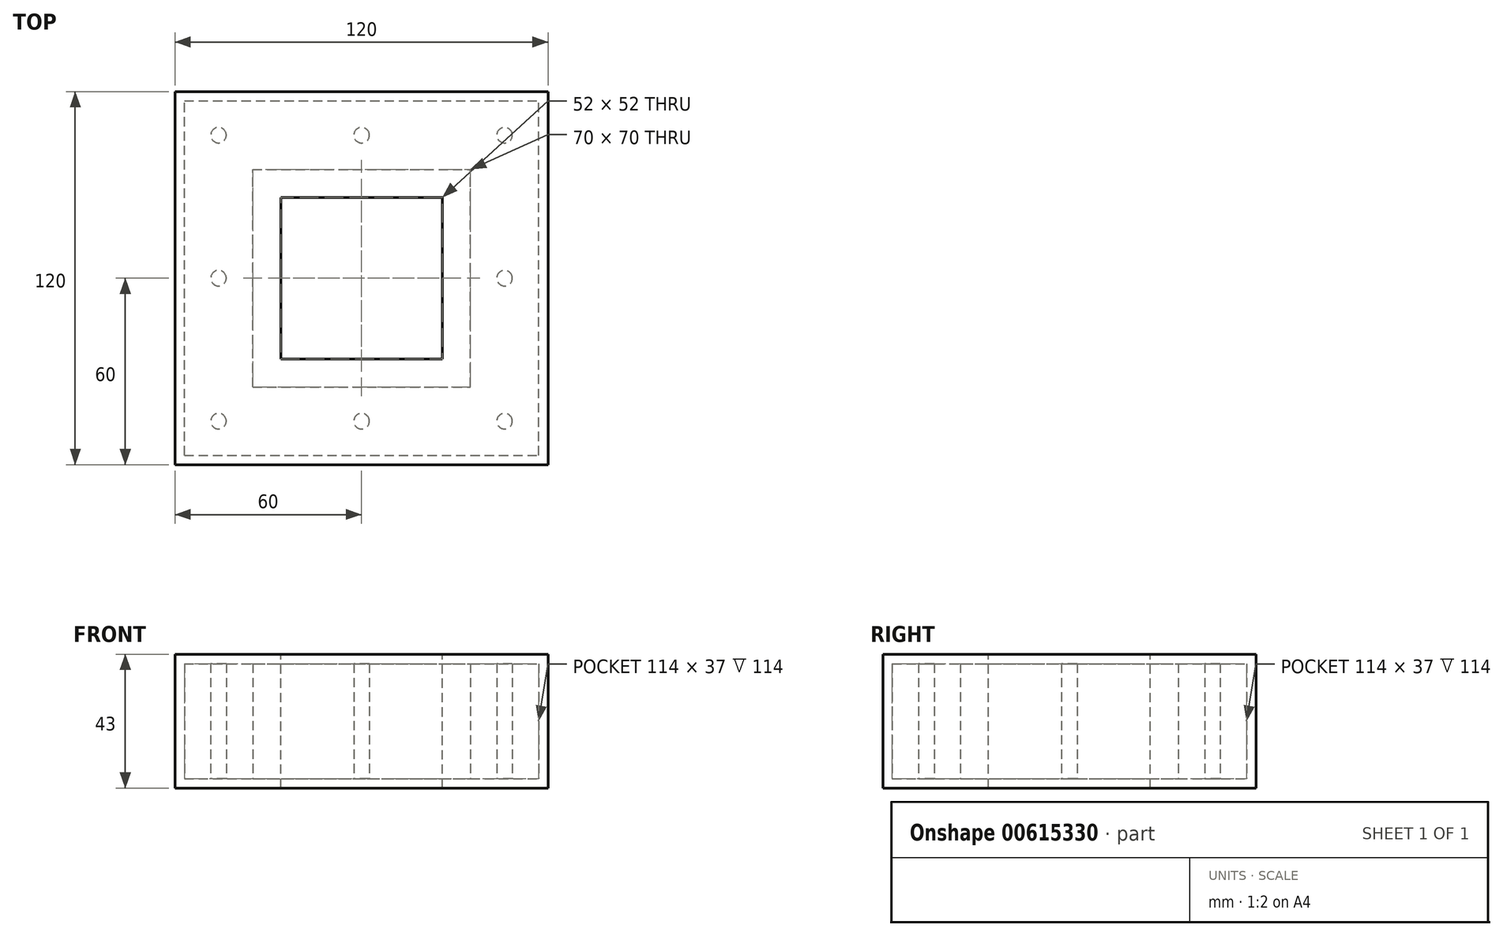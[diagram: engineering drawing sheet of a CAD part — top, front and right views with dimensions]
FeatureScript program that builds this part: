
annotation { "Feature Type Name" : "Feature", "Feature Type Description" : "" }
export const myFeature = defineFeature(function(context is Context, id is Id, definition is map)
    precondition{}
    {
        {
            var Q0;
            Q0=qCreatedBy(makeId("Top.planeOp"),FACE);
            var sketch = newSketch(context, id + "F0", { "sketchPlane" : qUnion([Q0])});
            skLineSegment(sketch, "E0.bottom", {"start": v(-60, -60) * mm, "end": v(60, -60) * mm});
            skLineSegment(sketch, "E0.top", {"start": v(-60, 60) * mm, "end": v(60, 60) * mm});
            skLineSegment(sketch, "E0.left", {"start": v(-60, -60) * mm, "end": v(-60, 60) * mm});
            skLineSegment(sketch, "E0.right", {"start": v(60, -60) * mm, "end": v(60, 60) * mm});
            skPoint(sketch, "E0.middle", {"position": v(0, 0) * mm});
            skSolve(sketch);
        }
        {
            var Q0;
            Q0 = qSketchRegion(id + "F0", true);
            extrude(context, id + "F1", {"entities" : qUnion([Q0]), "depth" : 3 * mm, "offsetDistance" : 25 * mm});
        }
        {
            var Q0;
            Q0=makeQuery(id+"F1.opExtrude","CAP_FACE",FACE,{"disambiguationData":[OSD([sQuery(id+"F0.wireOp",EDGE,"E0.bottom"),sQuery(id+"F0.wireOp",EDGE,"E0.top"),sQuery(id+"F0.wireOp",EDGE,"E0.left"),sQuery(id+"F0.wireOp",EDGE,"E0.right")])],"isStart":false});
            var sketch = newSketch(context, id + "F2", { "sketchPlane" : qUnion([Q0])});
            skLineSegment(sketch, "E1.bottom", {"start": v(-26, -26) * mm, "end": v(26, -26) * mm});
            skLineSegment(sketch, "E1.top", {"start": v(-26, 26) * mm, "end": v(26, 26) * mm});
            skLineSegment(sketch, "E1.left", {"start": v(-26, -26) * mm, "end": v(-26, 26) * mm});
            skLineSegment(sketch, "E1.right", {"start": v(26, -26) * mm, "end": v(26, 26) * mm});
            skPoint(sketch, "E1.middle", {"position": v(0, 0) * mm});
            skLineSegment(sketch, "E2.bottom", {"start": v(-35, -35) * mm, "end": v(35, -35) * mm});
            skLineSegment(sketch, "E2.top", {"start": v(-35, 35) * mm, "end": v(35, 35) * mm});
            skLineSegment(sketch, "E2.left", {"start": v(-35, -35) * mm, "end": v(-35, 35) * mm});
            skLineSegment(sketch, "E2.right", {"start": v(35, -35) * mm, "end": v(35, 35) * mm});
            skLineSegment(sketch, "E3.bottom", {"start": v(-57, -57) * mm, "end": v(57, -57) * mm});
            skLineSegment(sketch, "E3.top", {"start": v(-57, 57) * mm, "end": v(57, 57) * mm});
            skLineSegment(sketch, "E3.left", {"start": v(-57, -57) * mm, "end": v(-57, 57) * mm});
            skLineSegment(sketch, "E3.right", {"start": v(57, -57) * mm, "end": v(57, 57) * mm});
            skLineSegment(sketch, "E4", {"start": v(-57, 35) * mm, "end": v(-57, 57) * mm});
            skLineSegment(sketch, "E5", {"start": v(-35, 57) * mm, "end": v(-57, 57) * mm});
            skLineSegment(sketch, "E6", {"start": v(35, 35) * mm, "end": v(57, 35) * mm});
            skLineSegment(sketch, "E7", {"start": v(57, 35) * mm, "end": v(57, 57) * mm});
            skLineSegment(sketch, "E8", {"start": v(35, 57) * mm, "end": v(57, 57) * mm});
            skLineSegment(sketch, "E9", {"start": v(35, -35) * mm, "end": v(57, -35) * mm});
            skLineSegment(sketch, "E10", {"start": v(57, -35) * mm, "end": v(57, -57) * mm});
            skLineSegment(sketch, "E11", {"start": v(57, -57) * mm, "end": v(35, -57) * mm});
            skLineSegment(sketch, "E12", {"start": v(-35, -35) * mm, "end": v(-57, -35) * mm});
            skLineSegment(sketch, "E13", {"start": v(-57, -35) * mm, "end": v(-57, -57) * mm});
            skLineSegment(sketch, "E14", {"start": v(-57, -57) * mm, "end": v(-35, -57) * mm});
            skPoint(sketch, "E15", {"position": v(-46, 46) * mm});
            skPoint(sketch, "E15.positionSnap0", {"position": v(-57, 46) * mm});
            skPoint(sketch, "E15.positionSnap1", {"position": v(-46, 57) * mm});
            skPoint(sketch, "E16", {"position": v(46, 46) * mm});
            skPoint(sketch, "E16.positionSnap0", {"position": v(57, 46) * mm});
            skPoint(sketch, "E16.positionSnap1", {"position": v(46, 57) * mm});
            skPoint(sketch, "E17", {"position": v(46, -46) * mm});
            skPoint(sketch, "E17.positionSnap0", {"position": v(57, -46) * mm});
            skPoint(sketch, "E17.positionSnap1", {"position": v(46, 35) * mm});
            skPoint(sketch, "E18", {"position": v(-46, -46) * mm});
            skPoint(sketch, "E18.positionSnap0", {"position": v(-46, -57) * mm});
            skPoint(sketch, "E18.positionSnap1", {"position": v(-57, -46) * mm});
            skPoint(sketch, "E19", {"position": v(0, -46) * mm});
            skPoint(sketch, "E19.positionSnap0", {"position": v(0, -57) * mm});
            skPoint(sketch, "E20", {"position": v(0, 46) * mm});
            skPoint(sketch, "E20.positionSnap0", {"position": v(0, 57) * mm});
            skCircle(sketch, "E21", {"center": v(-46, 46) * mm, "radius": 2.5 * mm});
            skCircle(sketch, "E22", {"center": v(0, 46) * mm, "radius": 2.5 * mm});
            skCircle(sketch, "E23", {"center": v(46, 46) * mm, "radius": 2.5 * mm});
            skCircle(sketch, "E24", {"center": v(46, -46) * mm, "radius": 2.5 * mm});
            skCircle(sketch, "E25", {"center": v(0, -46) * mm, "radius": 2.5 * mm});
            skCircle(sketch, "E26", {"center": v(-46, -46) * mm, "radius": 2.5 * mm});
            skCircle(sketch, "E27", {"center": v(46, 0) * mm, "radius": 2.5 * mm});
            skCircle(sketch, "E28", {"center": v(-46, 0) * mm, "radius": 2.5 * mm});
            skSolve(sketch);
        }
        {
            var Q0;
            Q0=makeQuery(id+"F2.imprint","IMPRINT",FACE,{"disambiguationData":[TD([[makeQuery(id+"F2.imprint","IMPRINT",EDGE,{"derivedFrom":sQuery(id+"F2.wireOp",EDGE,"E1.bottom")}),1.0]])]});
            extrude(context, id + "F3", {"entities" : qUnion([Q0]), "operationType" : NewBodyOperationType.REMOVE, "oppositeDirection" : true, "depth" : 25 * mm, "offsetDistance" : 25 * mm});
        }
        {
            var Q0;
            Q0=makeQuery(id+"F2.imprint","IMPRINT",FACE,{"disambiguationData":[TD([[makeQuery(id+"F2.imprint","IMPRINT",EDGE,{"derivedFrom":sQuery(id+"F2.wireOp",EDGE,"E23")}),1.0]])]});
            var Q1;
            Q1=makeQuery(id+"F2.imprint","IMPRINT",FACE,{"disambiguationData":[TD([[makeQuery(id+"F2.imprint","IMPRINT",EDGE,{"derivedFrom":sQuery(id+"F2.wireOp",EDGE,"E22")}),1.0]])]});
            var Q2;
            Q2=makeQuery(id+"F2.imprint","IMPRINT",FACE,{"disambiguationData":[TD([[makeQuery(id+"F2.imprint","IMPRINT",EDGE,{"derivedFrom":sQuery(id+"F2.wireOp",EDGE,"E21")}),1.0]])]});
            var Q3;
            Q3=makeQuery(id+"F2.imprint","IMPRINT",FACE,{"disambiguationData":[TD([[makeQuery(id+"F2.imprint","IMPRINT",EDGE,{"derivedFrom":sQuery(id+"F2.wireOp",EDGE,"E28")}),1.0]])]});
            var Q4;
            Q4=makeQuery(id+"F2.imprint","IMPRINT",FACE,{"disambiguationData":[TD([[makeQuery(id+"F2.imprint","IMPRINT",EDGE,{"derivedFrom":sQuery(id+"F2.wireOp",EDGE,"E26")}),1.0]])]});
            var Q5;
            Q5=makeQuery(id+"F2.imprint","IMPRINT",FACE,{"disambiguationData":[TD([[makeQuery(id+"F2.imprint","IMPRINT",EDGE,{"derivedFrom":sQuery(id+"F2.wireOp",EDGE,"E25")}),1.0]])]});
            var Q6;
            Q6=makeQuery(id+"F2.imprint","IMPRINT",FACE,{"disambiguationData":[TD([[makeQuery(id+"F2.imprint","IMPRINT",EDGE,{"derivedFrom":sQuery(id+"F2.wireOp",EDGE,"E24")}),1.0]])]});
            var Q7;
            Q7=makeQuery(id+"F2.imprint","IMPRINT",FACE,{"disambiguationData":[TD([[makeQuery(id+"F2.imprint","IMPRINT",EDGE,{"derivedFrom":sQuery(id+"F2.wireOp",EDGE,"E27")}),1.0]])]});
            var Q8;
            Q8=makeQuery(id+"F2.imprint","IMPRINT",FACE,{"disambiguationData":[TD([[makeQuery(id+"F2.imprint","IMPRINT",EDGE,{"derivedFrom":sQuery(id+"F2.wireOp",EDGE,"E3.bottom")}),-1.0]])]});
            var Q9;
            Q9=makeQuery(id+"F2.imprint","IMPRINT",FACE,{"disambiguationData":[TD([[makeQuery(id+"F2.imprint","IMPRINT",EDGE,{"derivedFrom":sQuery(id+"F2.wireOp",EDGE,"E1.bottom")}),-1.0]])]});
            extrude(context, id + "F4", {"entities" : qUnion([Q0, Q1, Q2, Q3, Q4, Q5, Q6, Q7, Q8, Q9]), "operationType" : NewBodyOperationType.ADD, "depth" : 37 * mm, "offsetDistance" : 25 * mm});
        }
        {
            var Q0;
            Q0=makeQuery(id+"F4.opExtrude","CAP_FACE",FACE,{"disambiguationData":[OSD([sQuery(id+"F0.wireOp",EDGE,"E0.bottom"),sQuery(id+"F0.wireOp",EDGE,"E0.top"),sQuery(id+"F0.wireOp",EDGE,"E0.left"),sQuery(id+"F0.wireOp",EDGE,"E0.right"),sQuery(id+"F2.wireOp",EDGE,"E3.bottom"),sQuery(id+"F2.wireOp",EDGE,"E3.top"),sQuery(id+"F2.wireOp",EDGE,"E3.left"),sQuery(id+"F2.wireOp",EDGE,"E3.right"),sQuery(id+"F2.wireOp",EDGE,"E4"),sQuery(id+"F2.wireOp",EDGE,"E7"),sQuery(id+"F2.wireOp",EDGE,"E8"),sQuery(id+"F2.wireOp",EDGE,"E5"),sQuery(id+"F2.wireOp",EDGE,"E10"),sQuery(id+"F2.wireOp",EDGE,"E11"),sQuery(id+"F2.wireOp",EDGE,"E13"),sQuery(id+"F2.wireOp",EDGE,"E14")])],"isStart":false});
            var sketch = newSketch(context, id + "F5", { "sketchPlane" : qUnion([Q0])});
            skPoint(sketch, "E29.middle", {"position": v(0, 0) * mm});
            skLineSegment(sketch, "E30", {"start": v(-60, 60) * mm, "end": v(-60, -60) * mm});
            skLineSegment(sketch, "E31", {"start": v(-60, -60) * mm, "end": v(60, -60) * mm});
            skLineSegment(sketch, "E32", {"start": v(60, -60) * mm, "end": v(60, 60) * mm});
            skLineSegment(sketch, "E33", {"start": v(60, 60) * mm, "end": v(-60, 60) * mm});
            skLineSegment(sketch, "E34.bottom", {"start": v(-26, -26) * mm, "end": v(26, -26) * mm});
            skLineSegment(sketch, "E34.top", {"start": v(-26, 26) * mm, "end": v(26, 26) * mm});
            skLineSegment(sketch, "E34.left", {"start": v(-26, -26) * mm, "end": v(-26, 26) * mm});
            skLineSegment(sketch, "E34.right", {"start": v(26, -26) * mm, "end": v(26, 26) * mm});
            skSolve(sketch);
        }
        {
            var Q0;
            Q0=makeQuery(id+"F5.imprint","IMPRINT",FACE,{"disambiguationData":[TD([[makeQuery(id+"F5.imprint","IMPRINT",EDGE,{"derivedFrom":sQuery(id+"F5.wireOp",EDGE,"E34.bottom")}),-1.0]])]});
            var Q1;
            Q1=makeQuery(id+"F5.imprint","IMPRINT",FACE,{"disambiguationData":[TD([[makeQuery(id+"F5.imprint","IMPRINT",EDGE,{"derivedFrom":sQuery(id+"F5.wireOp",EDGE,"E30")}),-1.0]])]});
            extrude(context, id + "F6", {"entities" : qUnion([Q0, Q1]), "operationType" : NewBodyOperationType.ADD, "depth" : 3 * mm, "offsetDistance" : 25 * mm});
        }
    });
